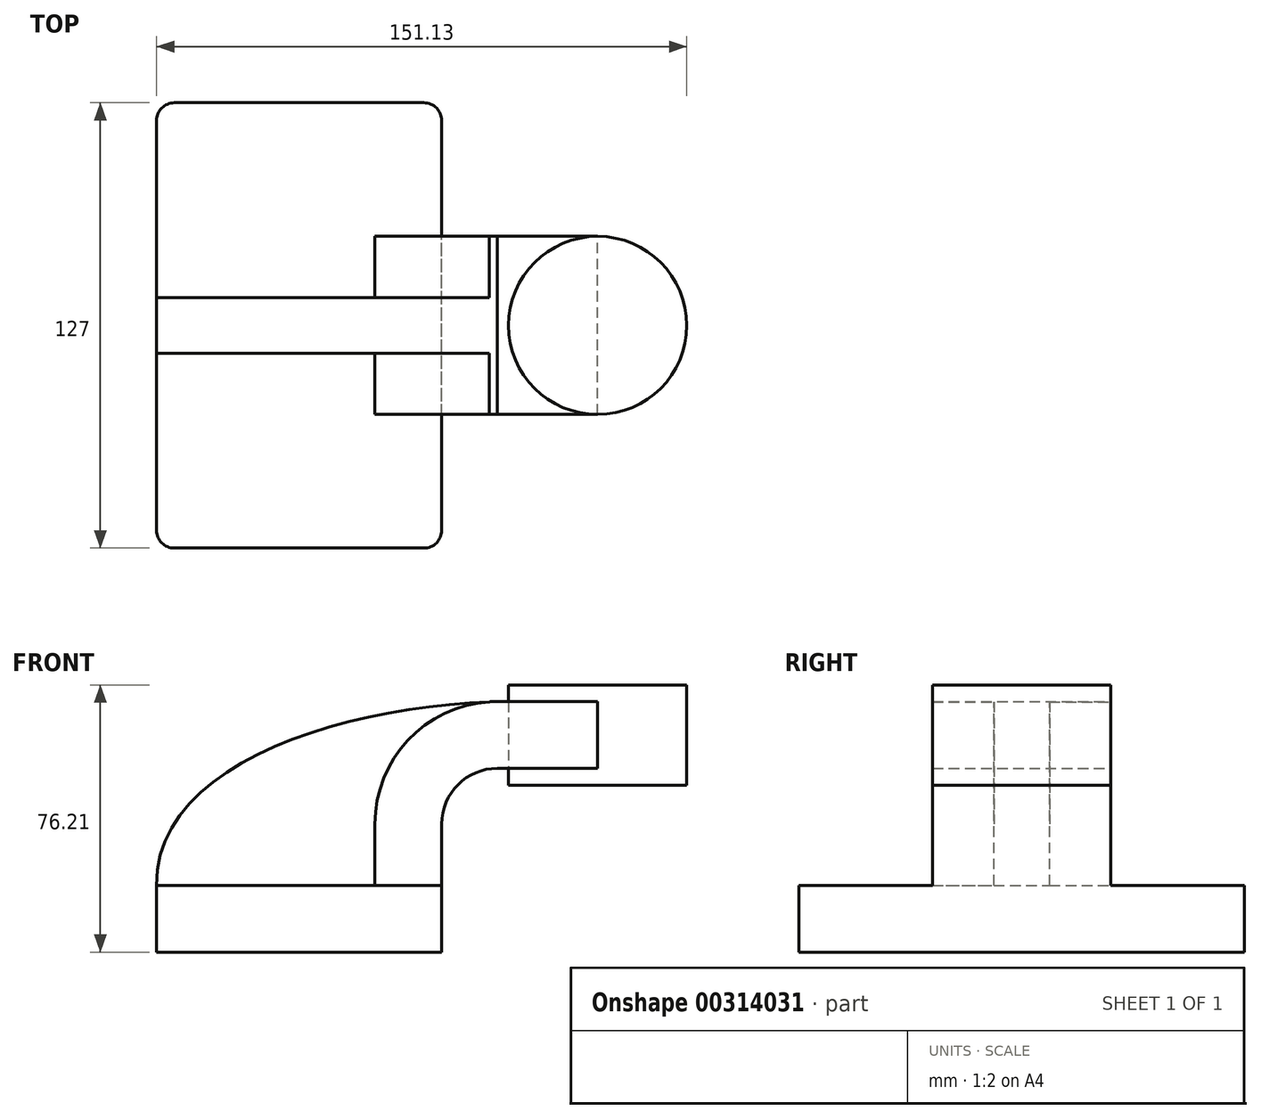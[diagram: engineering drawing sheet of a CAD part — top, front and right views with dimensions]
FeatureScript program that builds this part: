
annotation { "Feature Type Name" : "Feature", "Feature Type Description" : "" }
export const myFeature = defineFeature(function(context is Context, id is Id, definition is map)
    precondition{}
    {
        {
            var Q0;
            Q0=qCreatedBy(makeId("Front.planeOp"),FACE);
            var sketch = newSketch(context, id + "F0", { "sketchPlane" : qUnion([Q0])});
            skLineSegment(sketch, "E0.bottom", {"start": v(40.64, -9.52) * mm, "end": v(-40.64, -9.53) * mm});
            skLineSegment(sketch, "E0.top", {"start": v(40.64, 9.53) * mm, "end": v(-40.64, 9.53) * mm});
            skLineSegment(sketch, "E0.left", {"start": v(40.64, -9.52) * mm, "end": v(40.64, 9.53) * mm});
            skLineSegment(sketch, "E0.right", {"start": v(-40.64, -9.53) * mm, "end": v(-40.64, 9.53) * mm});
            skPoint(sketch, "E0.middle", {"position": v(0, 0) * mm});
            skLineSegment(sketch, "E1.bottom", {"start": v(110.49, 38.1) * mm, "end": v(59.69, 38.1) * mm});
            skLineSegment(sketch, "E1.top", {"start": v(110.5, 66.68) * mm, "end": v(59.69, 66.68) * mm});
            skLineSegment(sketch, "E1.left", {"start": v(110.5, 38.1) * mm, "end": v(110.5, 66.68) * mm});
            skLineSegment(sketch, "E1.right", {"start": v(59.69, 38.1) * mm, "end": v(59.69, 66.68) * mm});
            skPoint(sketch, "E1.middle", {"position": v(85.1, 52.39) * mm});
            skLineSegment(sketch, "E2", {"start": v(40.64, 9.53) * mm, "end": v(40.64, 27) * mm});
            skArc(sketch, "E3", {"start": v(56.52, 42.88) * mm, "mid": v(45.29, 38.23) * mm, "end": v(40.64, 27) * mm});
            skLineSegment(sketch, "E4", {"start": v(56.52, 42.88) * mm, "end": v(92.14, 42.88) * mm});
            skLineSegment(sketch, "E5.0", {"start": v(56.52, 61.93) * mm, "end": v(92.14, 61.93) * mm});
            skArc(sketch, "E5.1", {"start": v(56.52, 61.93) * mm, "mid": v(31.82, 51.7) * mm, "end": v(21.6, 27) * mm});
            skLineSegment(sketch, "E5.2", {"start": v(21.59, 9.53) * mm, "end": v(21.59, 27) * mm});
            skFitSpline(sketch, "E6", {"points": [v(-40.64, 9.53) * mm, v(56.52, 61.93) * mm], "startDerivative": vector(-1.4, 104.88) * mm, "endDerivative": vector(130.1, 3.5) * mm});
            skLineSegment(sketch, "E7", {"start": v(85.1, 38.1) * mm, "end": v(85.1, 66.68) * mm});
            skSolve(sketch);
        }
        {
            var Q0;
            Q0=makeQuery(id+"F0.imprint","IMPRINT",FACE,{"disambiguationData":[TD([[makeQuery(id+"F0.imprint","IMPRINT",EDGE,{"derivedFrom":sQuery(id+"F0.wireOp",EDGE,"E0.bottom")}),-1.0]])]});
            extrude(context, id + "F1", {"entities" : qUnion([Q0]), "endBound" : BoundingType.SYMMETRIC, "depth" : 127 * mm});
        }
        {
            var Q0;
            {var subQ1=sQuery(id+"F0.wireOp",EDGE,"E2");Q0=makeQuery(id+"F0.imprint","IMPRINT",FACE,{"disambiguationData":[TD([[makeQuery(id+"F0.imprint","IMPRINT",EDGE,{"derivedFrom":subQ1}),1.0]])]});}
            var Q1;
            {var subQ0=sQuery(id+"F0.wireOp",EDGE,"E4");var subQ1=sQuery(id+"F0.wireOp",EDGE,"E1.right");var subQ2=makeQuery(id+"F0.imprint","INTERSECT",VERTEX,{"derivedFrom":[subQ1,subQ0]});Q1=makeQuery(id+"F0.imprint","IMPRINT",FACE,{"disambiguationData":[TD([[makeQuery(id+"F0.imprint","IMPRINT",EDGE,{"disambiguationData":[TD([[subQ2,-1.0]])],"derivedFrom":subQ1}),-1.0]])]});}
            extrude(context, id + "F2", {"entities" : qUnion([Q0, Q1]), "operationType" : NewBodyOperationType.ADD, "endBound" : BoundingType.SYMMETRIC, "depth" : 50.8 * mm});
        }
        {
            var Q0;
            {var subQ3=sQuery(id+"F0.wireOp",EDGE,"E5.2");Q0=makeQuery(id+"F0.imprint","IMPRINT",FACE,{"disambiguationData":[TD([[makeQuery(id+"F0.imprint","IMPRINT",EDGE,{"derivedFrom":subQ3}),1.0]])]});}
            extrude(context, id + "F3", {"entities" : qUnion([Q0]), "operationType" : NewBodyOperationType.ADD, "endBound" : BoundingType.SYMMETRIC, "depth" : 15.88 * mm});
        }
        {
            var Q0;
            {var subQ4=sQuery(id+"F0.wireOp",EDGE,"E1.left");Q0=makeQuery(id+"F0.imprint","IMPRINT",FACE,{"disambiguationData":[TD([[makeQuery(id+"F0.imprint","IMPRINT",EDGE,{"derivedFrom":subQ4}),1.0]])]});}
            var Q1;
            Q1=sQuery(id+"F0.wireOp",EDGE,"E7");
            revolve(context, id + "F4", {"entities" : qUnion([Q0]), "axis" : qUnion([Q1]), "revolveType" : RevolveType.FULL});
        }
        {
            var Q0;
            Q0=makeQuery(id+"F1.opExtrude","CAP_EDGE",EDGE,{"disambiguationData":[OSD([sQuery(id+"F0.wireOp",EDGE,"E0.left")])],"isStart":false});
            var Q1;
            Q1=makeQuery(id+"F1.opExtrude","CAP_EDGE",EDGE,{"disambiguationData":[OSD([sQuery(id+"F0.wireOp",EDGE,"E0.right")])],"isStart":false});
            var Q2;
            Q2=makeQuery(id+"F1.opExtrude","CAP_EDGE",EDGE,{"disambiguationData":[OSD([sQuery(id+"F0.wireOp",EDGE,"E0.right")])],"isStart":true});
            var Q3;
            Q3=makeQuery(id+"F1.opExtrude","CAP_EDGE",EDGE,{"disambiguationData":[OSD([sQuery(id+"F0.wireOp",EDGE,"E0.left")])],"isStart":true});
            fillet(context, id + "F5", {"entities" : qUnion([Q0, Q1, Q2, Q3]), "radius" : 5.08 * mm, "tangentPropagation" : true, "allowEdgeOverflow" : false});
        }
    });
